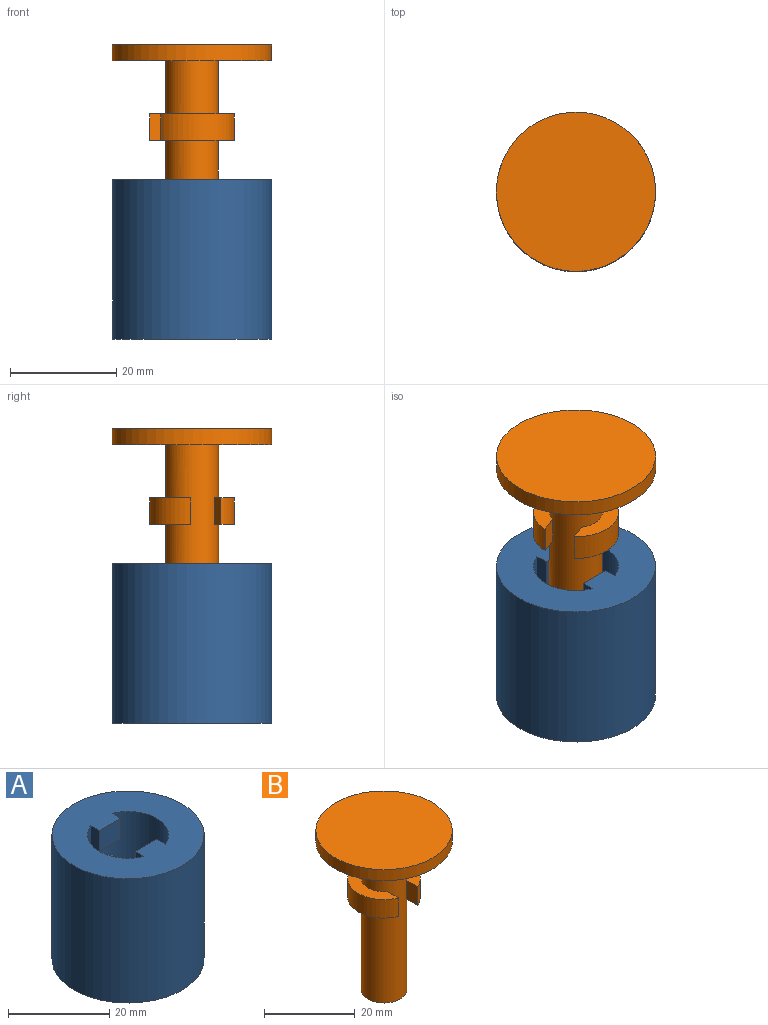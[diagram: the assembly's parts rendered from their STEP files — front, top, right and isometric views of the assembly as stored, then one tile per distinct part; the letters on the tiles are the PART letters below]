
ASSEMBLY  parts=2 mates=1
PART A: 20 faces, bbox 30x30x30 mm
  f0: plane 5x2.43mm, normal (-1,0,0), area 12.1mm2, adj f1,f6,f7,f18
  f1: plane 5.95x5mm, normal (0,1,0), area 29.8mm2, adj f0,f2,f6,f18
  f2: plane 5x2.43mm, normal (1,0,0), area 12.1mm2, adj f1,f6,f7,f18
  f3: plane 5x2.43mm, normal (1,0,0), area 12.1mm2, adj f4,f6,f7,f16
  f4: plane 5.95x5mm, normal (0,-1,0), area 29.8mm2, adj f3,f5,f6,f16
  f5: plane 5x2.43mm, normal (-1,0,0), area 12.1mm2, adj f4,f6,f7,f16
  f6: plane 30x30mm, normal (0,0,1), area 539.3mm2, adj f0,f1,f2,f3,f4,f5,f7,f9
  f7: cylinder r=8mm len=30mm, axis (0,0,1), area 1203.1mm2, adj f0,f2,f3,f5,f6,f8,f10,f12
  f8: plane 30x30mm, normal (0,0,-1), area 539.3mm2, adj f7,f9,f10,f11,f12,f13,f14,f15
  f9: cylinder r=15mm len=30mm, axis (0,0,1), area 2827.4mm2, adj f6,f8
  f10: plane 20x2.43mm, normal (-1,0,0), area 48.5mm2, adj f7,f8,f11,f19
  f11: plane 20x5.95mm, normal (0,1,0), area 119mm2, adj f8,f10,f12,f19
  f12: plane 20x2.43mm, normal (1,0,0), area 48.5mm2, adj f7,f8,f11,f19
  f13: plane 20x2.43mm, normal (1,0,0), area 48.5mm2, adj f7,f8,f14,f17
  f14: plane 20x5.95mm, normal (0,-1,0), area 119mm2, adj f8,f13,f15,f17
  f15: plane 20x2.43mm, normal (-1,0,0), area 48.5mm2, adj f7,f8,f14,f17
  f16: plane 5.95x3mm, normal (0,0,-1), area 16.7mm2, adj f3,f4,f5,f7
  f17: plane 5.95x3mm, normal (0,0,1), area 16.7mm2, adj f7,f13,f14,f15
  f18: plane 5.95x3mm, normal (0,0,-1), area 16.7mm2, adj f0,f1,f2,f7
  f19: plane 5.95x3mm, normal (0,0,1), area 16.7mm2, adj f7,f10,f11,f12
PART B: 15 faces, bbox 30x30x43 mm
  f0: cylinder r=8mm len=14.83mm, axis (0,0,1), area 94.9mm2, adj f1,f2,f12,f14
  f1: plane 14.83x5mm, normal (0,0,-1), area 42.5mm2, adj f0,f9,f12,f14
  f2: plane 14.83x5mm, normal (0,0,1), area 42.5mm2, adj f0,f9,f12,f14
  f3: cylinder r=8mm len=14.83mm, axis (0,0,1), area 94.9mm2, adj f7,f8,f11,f13
  f4: cylinder r=15mm len=30mm, axis (0,0,1), area 282.7mm2, adj f5,f10
  f5: plane 30x30mm, normal (0,0,1), area 706.9mm2, adj f4
  f6: plane 10x10mm, normal (0,0,-1), area 78.5mm2, adj f9
  f7: plane 14.83x5mm, normal (0,0,-1), area 42.5mm2, adj f3,f9,f11,f13
  f8: plane 14.83x5mm, normal (0,0,1), area 42.5mm2, adj f3,f9,f11,f13
  f9: cylinder r=5mm len=40mm, axis (0,0,1), area 1163.9mm2, adj f1,f2,f6,f7,f8,f10,f11,f12
  f10: plane 30x30mm, normal (0,0,-1), area 628.3mm2, adj f4,f9
  f11: plane 5x3.42mm, normal (1,0,0), area 17.1mm2, adj f3,f7,f8,f9
  f12: plane 5x3.42mm, normal (-1,0,0), area 17.1mm2, adj f0,f1,f2,f9
  f13: plane 5x3.42mm, normal (1,0,0), area 17.1mm2, adj f3,f7,f8,f9
  f14: plane 5x3.42mm, normal (-1,0,0), area 17.1mm2, adj f0,f1,f2,f9
PLACE A t=(-23.06,-33.21,-11.08)mm fixed
PLACE B rot(axis=(0,0,1),110.3deg) t=(-23.06,-33.21,11.34)mm
MATE cylindrical B.f0 <-> A.f7  axis (0,0,1) through (-23.06,-33.21,-8.66)mm
